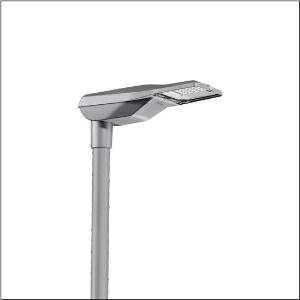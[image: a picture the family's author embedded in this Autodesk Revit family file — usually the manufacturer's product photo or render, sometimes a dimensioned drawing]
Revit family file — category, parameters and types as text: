
# Revit family: streetlight_sl_21_iq_micro___st1_5a_5xe1p41g08db_1f20
name_source: partatom
category: Lighting Fixtures
units: mm (PartAtom-declared; Revit-internal decimal feet)

## family parameters
Cut with Voids When Loaded = No
Host = Face
Light Source = No
Part Type = Normal
Room Calculation Point = No
Round Connector Dimension = Use Diameter
Shared = No

## types (1)
- --- (1 x LED, 4930 lm, 36.4 W, 4000K)
    Apparent Load = 36 VA
    CIE Flux Codes = 22 53 95 100 100
    Color Rendering = 70
    Color Temperature = 4000K
    Default Elevation = 1800 mm
    Description = Streetlight SL 21 iQ micro, mast luminaire, primary light control with lens, of PMMA, primary optical cover: cover, of toughened safety glass, transparent, light distribution: ST1.5a, light emission: direct distribution, primary light characteristic: asymmetric, installation type: post-top, side-entry, LED, High Power LED, rated luminous flux: 4.930lm, luminous efficacy: 135lm/W, light colour: 740, colour temperature: 4000K, control: Street-Remote, Auto-Match, Temp-Guard, Lumen-Switch, Night-Set, Smart-Wire, Light-Fading, Desk-Remote (wireless, voltage-free reading and setting of iQ features in the workshop via application-optimized NFC function/RFID function), optimised constant luminous flux control (CLO 2.0), pre-setting: linear dimming characteristic, mains connection: 220..240V, AC, 50/60Hz, start of lifetime: 36W, end of service life: 38W, reduction: 16W, luminaire housing, of diecast aluminium, powder-coated, Siteco® metallic grey (DB 702S), corrosivity category C5 mid according to DIN EN ISO 12944, please order mast flange separately, inclination adjustable: 0°, 5°, 10°, 15°, sealing non-destructively replaceable, multi-level sealing system, length: 528mm, width: 235mm, height: 110mm, mast flange for spigot size: 42mm (side-entry): 5XC10008XM4, 60/48mm (side-entry/post-top): 5XC10108XM2, 76/60mm (side-entry/post-top): 5XC10108XM1, protection rating (complete): IP66, insulation class (complete): insulation class II (safety insulation), certification: CE, ENEC, ENEC+, VDE, impact resistance: IK09, permissible operating ambient temperature for outdoor applications: -40..+50°C, standard-compliant lighting for roads and squares, packaging unit: 1 piece

Light Distribution: ST1.5a
    Height = 110 mm
    Lamp = 1 x LED
    Lamp Light Flux = 4930 lm
    Lamp Power = 36.4 W
    Lamp count = 1
    Length = 528 mm
    Luminous efficacy = 135 lm/W
    Manufacturer = Siteco
    ModVariant = No
    Model = 5XE1P41G08DB
    Number of Poles = 1
    OnlyDefault = Yes
    Power Factor = 1
    Product Name = Streetlight SL 21 iQ micro | ST1.5a
    Product group = mast luminaire | pylon top
    ProductGroupID = 6100
    Protection Class = Protection class II
    Protection Degree = IP 66
    RLX_Detail_Level = 1
    RLX_Emergency_Light_Flux = 0 lm
    RLX_Emergency_Type = 0
    RLX_Emergency_Type_DB = No
    RlxData = <blob elided: 103377 chars, md5=6caf2fab>
    Socket = socket
    Standby Power = 0 W
    System Light Flux = 4930 lm
    System Power = 36 W
    Type Comments = factory setting: luminous flux: 100 % | dim-lin: 254 | 715 mA
    Type Image = l_1006881.jpg
    URL = http://relux.com
    VarID = @adj_124159
    Voltage = 0 V
    Weight = 0.00 kg
    Width = 235 mm

## geometry (parser evidence)
native form markers: Blend x4, Sweep x10
no freeform markers — native parametric forms only
